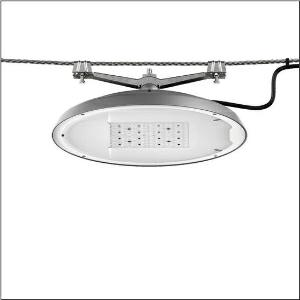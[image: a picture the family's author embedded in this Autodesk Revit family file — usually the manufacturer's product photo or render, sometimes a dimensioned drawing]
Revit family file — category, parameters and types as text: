
# Revit family: dl_r__50_iq_mini___st0_8s_5xa248v41f08me_8e0e
name_source: partatom
category: Lighting Fixtures
units: mm (PartAtom-declared; Revit-internal decimal feet)

## family parameters
Cut with Voids When Loaded = No
Host = Face
Light Source = No
Part Type = Normal
Room Calculation Point = No
Round Connector Dimension = Use Diameter
Shared = No

## types (1)
- --- (1 x LED, 15660 lm, 101.7 W, 4000K)
    Apparent Load = 102 VA
    CIE Flux Codes = 38 75 97 100 100
    Color Rendering = 70
    Color Temperature = 4000K
    Default Elevation = 1800 mm
    Description = DL® 50 iQ mini, catenary luminaire, primary light control with lens, of PMMA, primary optical cover: cover, of toughened safety glass, transparent, light distribution: ST0.8s, light emission: direct distribution, primary light characteristic: symmetric, installation type: suspended mounting, LED, High Power LED, rated luminous flux: 15.660lm, luminous efficacy: 154lm/W, light colour: 740, colour temperature: 4000K, control: optimised constant luminous flux control (CLO 2.0), Desk-Remote (wireless, voltage-free reading and setting of iQ features in the workshop via application-optimized NFC function/RFID function), Light-Fading, Smart-Wire, Night-Set, Lumen-Switch, Temp-Guard, Auto-Match, Street-Remote, mains connection: 230..240V, AC, 50/60Hz, start of lifetime: 102W, end of service life: 111W, reduction: 45W, luminaire housing, of diecast aluminium, powder-coated, Siteco® metallic grey (DB 702S), diameter: 500mm, height: 115mm, protection rating (complete): IP66, insulation class (complete): insulation class II (safety insulation), certification: CE, ENEC, ENEC+, VDE, impact resistance: IK08, permissible operating ambient temperature for outdoor applications: -25..+40°C, standard-compliant lighting for roads and squares, packaging unit: 1 piece

Light Distribution: ST0.8s
    Height = 124 mm  [stored 0.406824 ft]
    Lamp = 1 x LED
    Lamp Light Flux = 15660 lm
    Lamp Power = 101.7 W
    Lamp count = 1
    Length = 500 mm
    Luminous efficacy = 154 lm/W
    Manufacturer = Siteco
    ModVariant = No
    Model = 5XA248V41F08ME
    Number of Poles = 1
    OnlyDefault = Yes
    Power Factor = 1
    Product Name = DL® 50 iQ mini | ST0.8s
    Product group = catenary luminaire
    ProductGroupID = 6300
    Protection Class = Protection class II
    Protection Degree = IP 66
    RLX_Detail_Level = 1
    RLX_Emergency_Light_Flux = 0 lm
    RLX_Emergency_Type = 0
    RLX_Emergency_Type_DB = No
    RlxData = <blob elided: 127017 chars, md5=f3b9930a>
    Socket = socket
    Standby Power = 0 W
    System Light Flux = 15660 lm
    System Power = 102 W
    Type Comments = factory setting: luminous flux: 100 % | dim-lin: 254 | 534 mA
    Type Image = l_1251783.jpg
    URL = http://relux.com
    VarID = @adj_110747
    Voltage = 0 V
    Weight = 0.00 kg
    Width = 0 mm  [stored 0 ft]

note: [stored X ft] marks values corroborated as IEEE doubles in the binary element streams (Revit-internal decimal feet)

## geometry (parser evidence)
native form markers: Blend x4, Sweep x16
no freeform markers — native parametric forms only
